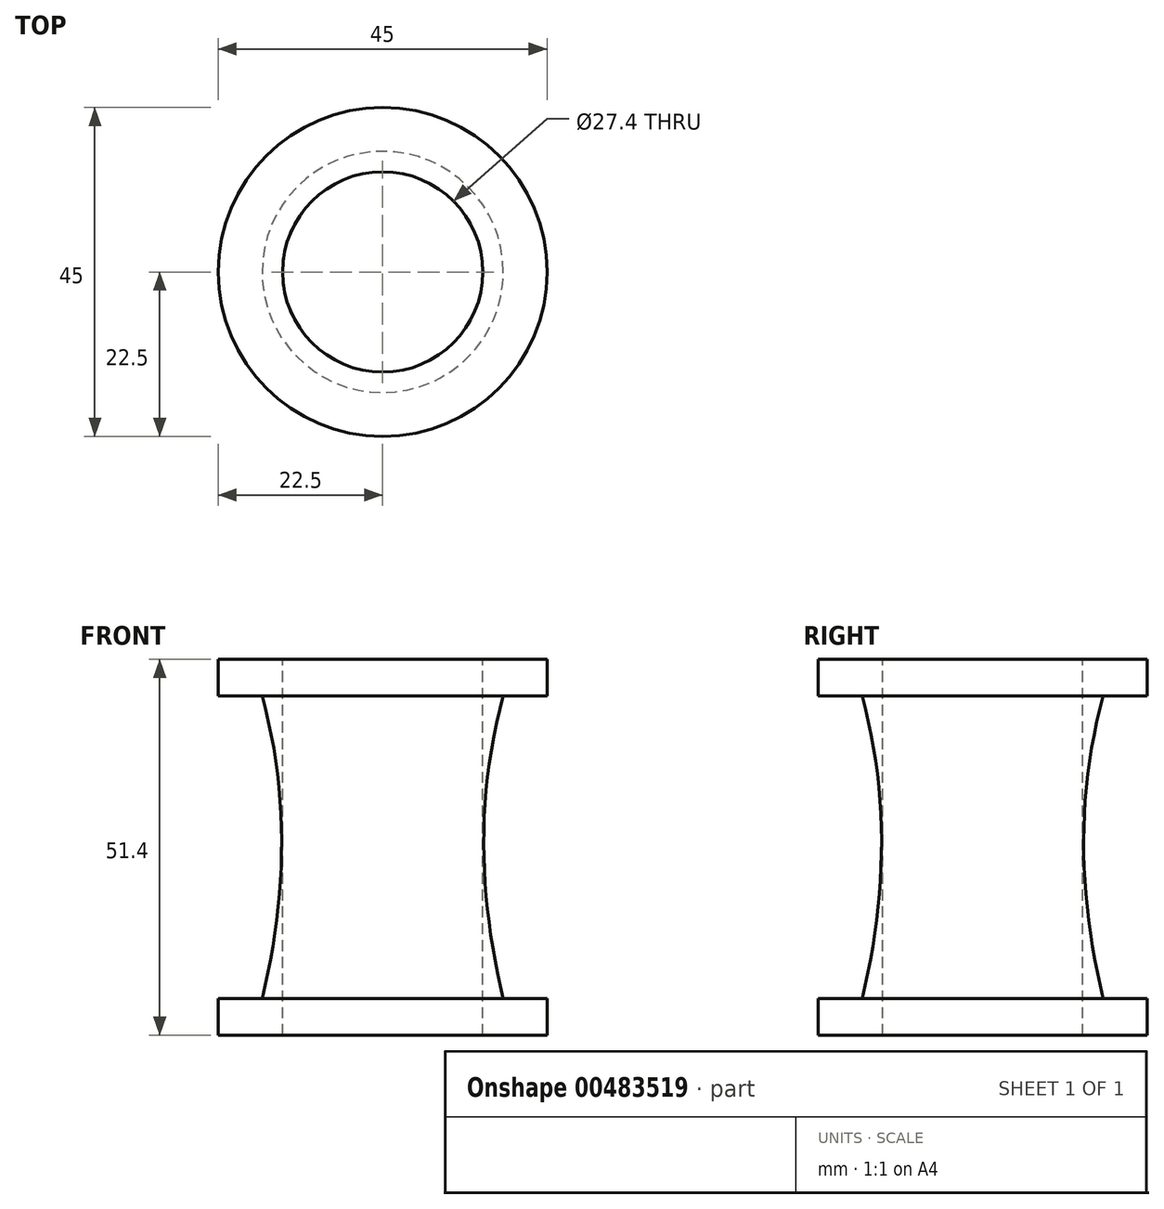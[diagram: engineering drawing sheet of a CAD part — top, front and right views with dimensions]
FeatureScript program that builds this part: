
annotation { "Feature Type Name" : "Feature", "Feature Type Description" : "" }
export const myFeature = defineFeature(function(context is Context, id is Id, definition is map)
    precondition{}
    {
        {
            var Q0;
            Q0=qCreatedBy(makeId("Front.planeOp"),FACE);
            var sketch = newSketch(context, id + "F0", { "sketchPlane" : qUnion([Q0])});
            skLineSegment(sketch, "E0", {"start": v(0, 0) * mm, "end": v(0, -25.7) * mm});
            skLineSegment(sketch, "E1", {"start": v(0, -25.7) * mm, "end": v(-22.5, -25.7) * mm});
            skLineSegment(sketch, "E2", {"start": v(-22.5, -25.7) * mm, "end": v(-22.5, -20.7) * mm});
            skLineSegment(sketch, "E3", {"start": v(-22.5, 25.7) * mm, "end": v(-22.5, 20.7) * mm});
            skLineSegment(sketch, "E4", {"start": v(-22.5, 25.7) * mm, "end": v(0, 25.7) * mm});
            skLineSegment(sketch, "E5", {"start": v(0, 25.7) * mm, "end": v(0, 0) * mm});
            skLineSegment(sketch, "E6", {"start": v(-16.5, -20.7) * mm, "end": v(-22.5, -20.7) * mm});
            skLineSegment(sketch, "E7", {"start": v(-16.5, 20.7) * mm, "end": v(-22.5, 20.7) * mm});
            skFitSpline(sketch, "E8", {"points": [v(-16.5, 20.7) * mm, v(-16.5, -20.7) * mm], "startDerivative": vector(11.73, -42.81) * mm, "endDerivative": vector(-9.59, -39.6) * mm});
            skSolve(sketch);
        }
        {
            var Q0;
            Q0=makeQuery(id+"F0.imprint","IMPRINT",FACE,{"disambiguationData":[TD([[makeQuery(id+"F0.imprint","IMPRINT",EDGE,{"derivedFrom":sQuery(id+"F0.wireOp",EDGE,"E0")}),-1.0]])]});
            var Q1;
            Q1=sQuery(id+"F0.wireOp",EDGE,"E0");
            revolve(context, id + "F1", {"entities" : qUnion([Q0]), "axis" : qUnion([Q1]), "revolveType" : RevolveType.FULL});
        }
        {
            var Q0;
            Q0=makeQuery(id+"F1.opRevolve","SWEPT_FACE",FACE,{"disambiguationData":[OSD([sQuery(id+"F0.wireOp",EDGE,"E4")])]});
            var sketch = newSketch(context, id + "F2", { "sketchPlane" : qUnion([Q0])});
            skCircle(sketch, "E9", {"center": v(0, 0) * mm, "radius": 13.7 * mm});
            skSolve(sketch);
        }
        {
            var Q0;
            Q0=qSketchRegion(id+"F2",true);
            var Q1;
            Q1=makeQuery(id+"F1.opRevolve","SWEPT_FACE",FACE,{"disambiguationData":[OSD([sQuery(id+"F0.wireOp",EDGE,"E1")])]});
            extrude(context, id + "F3", {"entities" : qUnion([Q0]), "operationType" : NewBodyOperationType.REMOVE, "endBound" : BoundingType.UP_TO_SURFACE, "oppositeDirection" : true, "endBoundEntityFace" : qUnion([Q1]), "depth" : 53.3 * mm});
        }
    });
